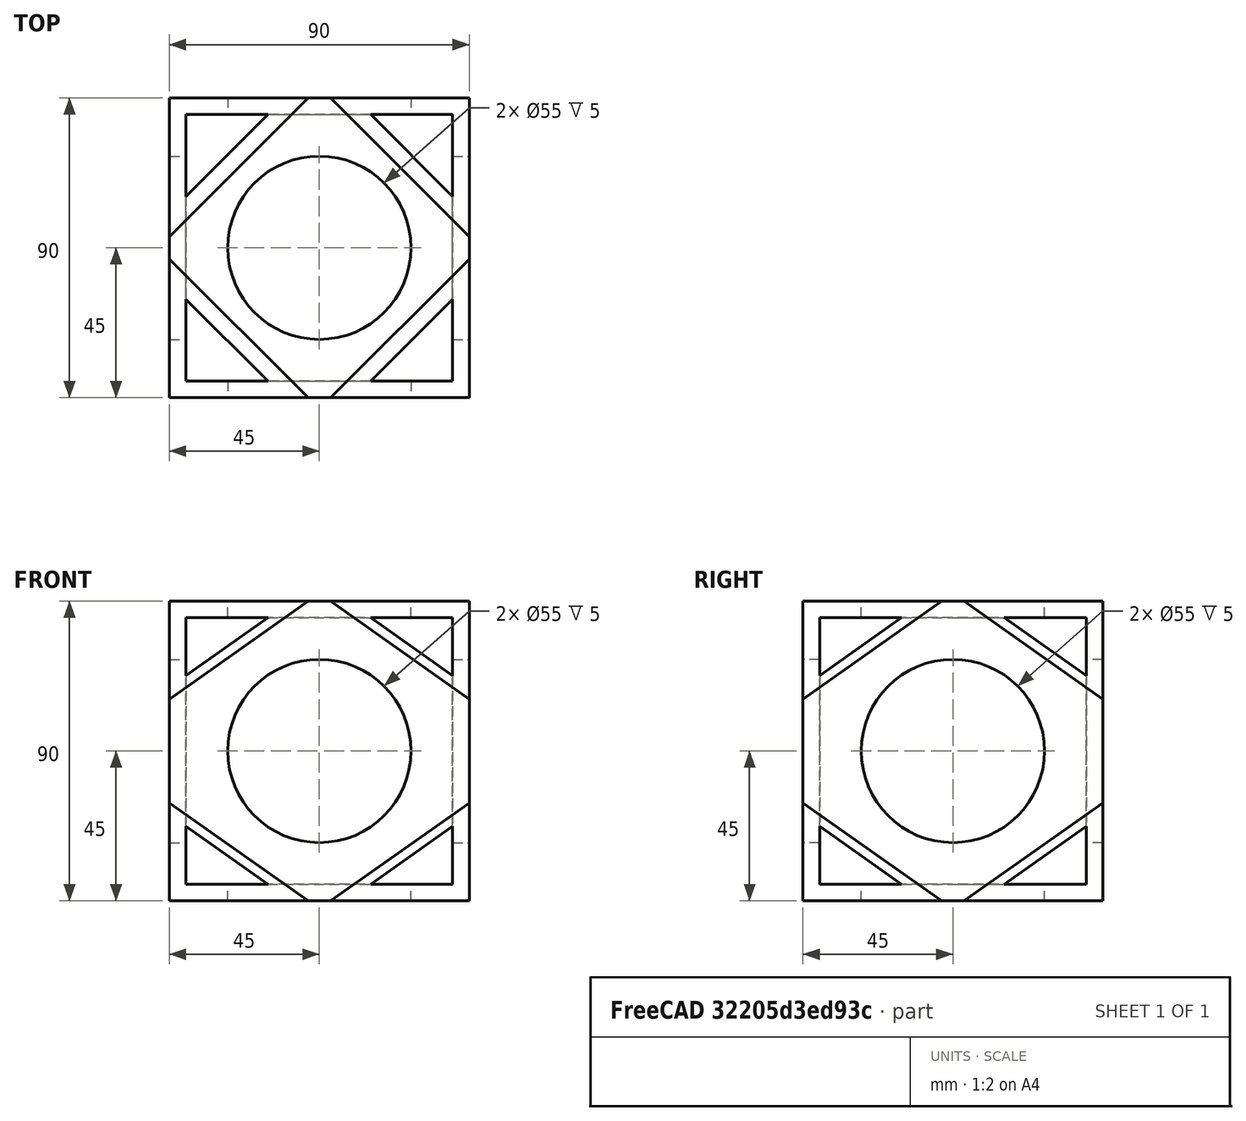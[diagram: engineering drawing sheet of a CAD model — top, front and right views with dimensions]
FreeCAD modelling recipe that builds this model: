
FCSTD DOCUMENT  (FreeCAD 0.17R13541 (Git))
Label: 201905231
License: All rights reserved
LicenseURL: http://en.wikipedia.org/wiki/All_rights_reserved
objects: Part::Box×6, Part::Cut×5, Part::Cylinder×3, Part::MultiFuse×1
note: 15 computed .brp shape members not serialized (recipe doc carries the construction recipe); baked Part::Feature solids carry a one-line shape summary decoded from their .brp

FEATURE [Part::Box] Box  label="立方体"
  AttacherType = Attacher::AttachEngine3D
  Height = 90
  Length = 90
  Placement = pos=(-45,-45,-45) rot=(0,0,1;0rad)
  Width = 90
FEATURE [Part::Box] Box001  label="立方体001"
  AttacherType = Attacher::AttachEngine3D
  Height = 80
  Length = 80
  Placement = pos=(-40,-40,-40) rot=(0,0,1;0rad)
  Width = 80
FEATURE [Part::Cylinder] Cylinder  label="圆柱体"
  Angle = 360
  AttacherType = Attacher::AttachEngine3D
  Height = 120
  Placement = pos=(0,0,-60) rot=(0,0,1;0rad)
  Radius = 27.5
FEATURE [Part::Cylinder] Cylinder001  label="圆柱体001"
  Angle = 360
  AttacherType = Attacher::AttachEngine3D
  Height = 120
  Placement = pos=(0,60,0) rot=(1,0,0;1.5708rad)
  Radius = 27.5
FEATURE [Part::Cylinder] Cylinder002  label="圆柱体002"
  Angle = 360
  AttacherType = Attacher::AttachEngine3D
  Height = 120
  Placement = pos=(-60,0,0) rot=(0,1,0;1.5708rad)
  Radius = 27.5
FEATURE [Part::MultiFuse] Fusion
  Shapes = -> [Box001,Cylinder,Cylinder001,Cylinder002]
FEATURE [Part::Cut] Cut
  Base = -> Box
  Tool = -> Fusion
FEATURE [Part::Box] Box002  label="立方体002"
  AttacherType = Attacher::AttachEngine3D
  Height = 112
  Length = 140
  Placement = pos=(-49.4975,-49.4975,-79.196) rot=(0.678598,0.281085,0.678598;1.09606rad)
  Width = 112
FEATURE [Part::Box] Box003  label="立方体003"
  AttacherType = Attacher::AttachEngine3D
  Height = 180
  Length = 180
  Placement = pos=(-63.6396,-63.6396,-127.279) rot=(0.678598,0.281085,0.678598;1.09606rad)
  Width = 180
FEATURE [Part::Box] Box004  label="立方体004"
  AttacherType = Attacher::AttachEngine3D
  Height = 112
  Length = 140
  Placement = pos=(-49.4975,49.4975,-79.196) rot=(-0.678598,0.281085,0.678598;5.18713rad)
  Width = 112
FEATURE [Part::Box] Box005  label="立方体005"
  AttacherType = Attacher::AttachEngine3D
  Height = 180
  Length = 180
  Placement = pos=(-63.6396,63.6396,-127.279) rot=(-0.678598,0.281085,0.678598;5.18713rad)
  Width = 180
FEATURE [Part::Cut] Cut001
  Base = -> Box003
  Tool = -> Box002
FEATURE [Part::Cut] Cut002
  Base = -> Box005
  Tool = -> Box004
FEATURE [Part::Cut] Cut003
  Base = -> Cut
  Tool = -> Cut001
FEATURE [Part::Cut] Cut004
  Base = -> Cut003
  Tool = -> Cut002
